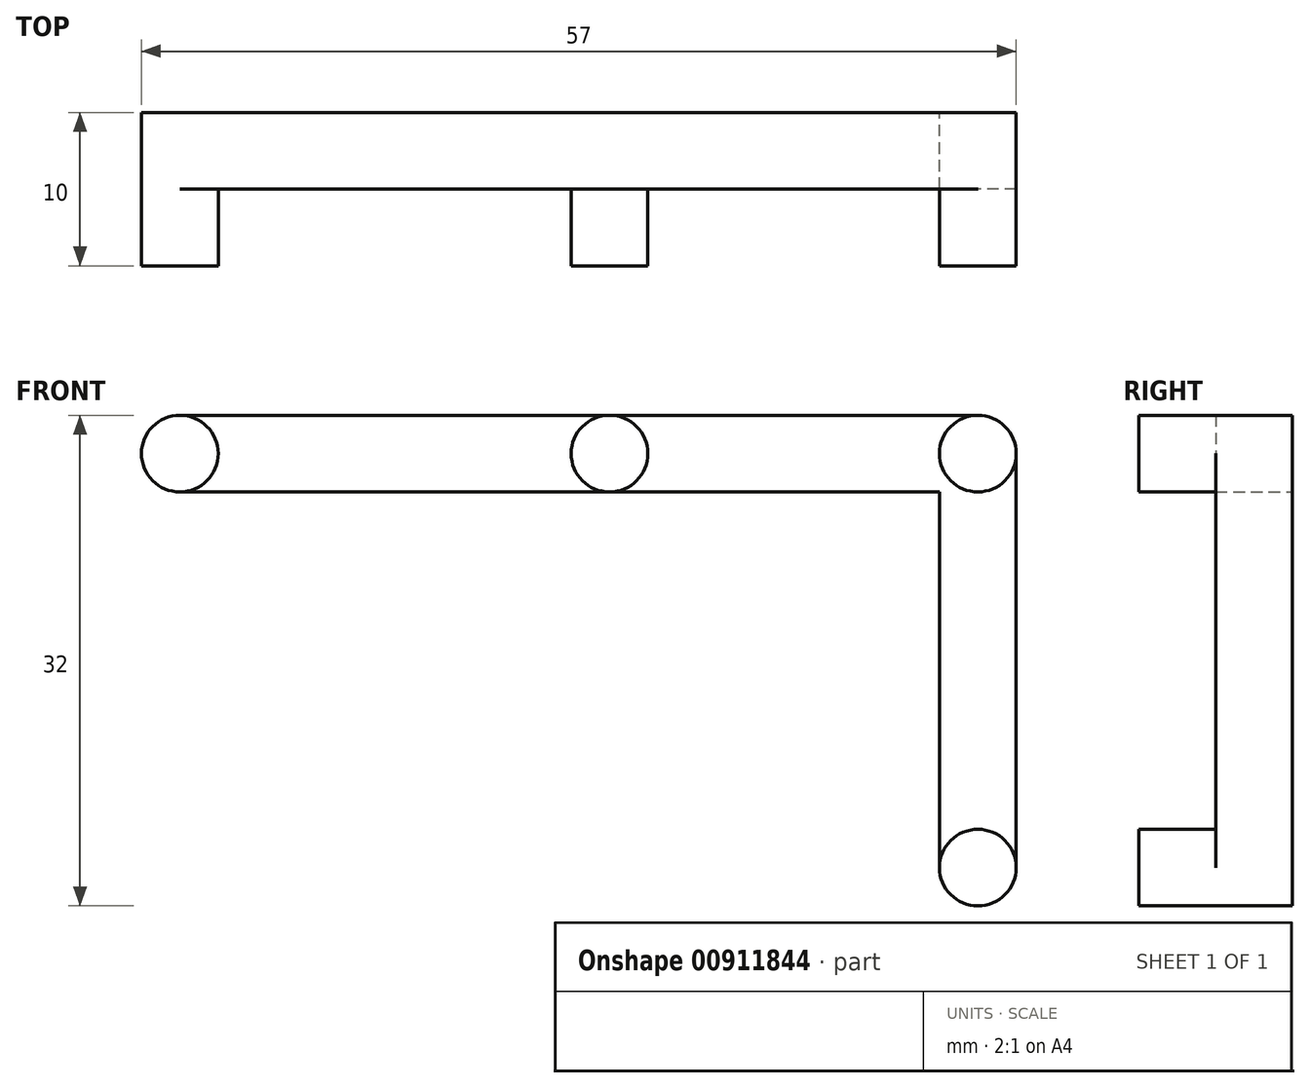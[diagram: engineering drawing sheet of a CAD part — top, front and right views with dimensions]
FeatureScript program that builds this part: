
annotation { "Feature Type Name" : "Feature", "Feature Type Description" : "" }
export const myFeature = defineFeature(function(context is Context, id is Id, definition is map)
    precondition{}
    {
        {
            var Q0;
            Q0=qCreatedBy(makeId("Front.planeOp"),FACE);
            var sketch = newSketch(context, id + "F0", { "sketchPlane" : qUnion([Q0])});
            skCircle(sketch, "E0", {"center": v(0, 0) * mm, "radius": 2.5 * mm});
            skCircle(sketch, "E1", {"center": v(28, 0) * mm, "radius": 2.5 * mm});
            skCircle(sketch, "E2", {"center": v(52, 0) * mm, "radius": 2.5 * mm});
            skCircle(sketch, "E3", {"center": v(52, -27) * mm, "radius": 2.5 * mm});
            skLineSegment(sketch, "E4.bottom", {"start": v(0, 2.5) * mm, "end": v(52, 2.5) * mm});
            skLineSegment(sketch, "E4.top", {"start": v(0, -2.5) * mm, "end": v(52, -2.5) * mm});
            skLineSegment(sketch, "E4.left", {"start": v(0, 2.5) * mm, "end": v(0, -2.5) * mm});
            skLineSegment(sketch, "E4.right", {"start": v(52, 2.5) * mm, "end": v(52, -2.5) * mm});
            skLineSegment(sketch, "E5.bottom", {"start": v(49.5, 0) * mm, "end": v(54.5, 0) * mm});
            skLineSegment(sketch, "E5.top", {"start": v(49.5, -27) * mm, "end": v(54.5, -27) * mm});
            skLineSegment(sketch, "E5.left", {"start": v(49.5, 0) * mm, "end": v(49.5, -27) * mm});
            skLineSegment(sketch, "E5.right", {"start": v(54.5, 0) * mm, "end": v(54.5, -27) * mm});
            skSolve(sketch);
        }
        {
            var Q0;
            Q0 = qSketchRegion(id + "F0", true);
            var Q1;
            {var subQ0=sQuery(id+"F0.wireOp",EDGE,"E4.right");var subQ3=sQuery(id+"F0.wireOp",EDGE,"E5.bottom");var subQ5=makeQuery(id+"F0.imprint","INTERSECT",VERTEX,{"derivedFrom":[subQ0,subQ3]});Q1=makeQuery(id+"F0.imprint","IMPRINT",FACE,{"disambiguationData":[TD([[makeQuery(id+"F0.imprint","IMPRINT",EDGE,{"disambiguationData":[TD([[subQ5,-1.0]])],"derivedFrom":subQ0}),-1.0]])]});}
            extrude(context, id + "F1", {"entities" : qUnion([Q0, Q1]), "depth" : 5 * mm, "offsetDistance" : 25 * mm});
        }
        {
            var Q0;
            {var subQ0=sQuery(id+"F0.wireOp",EDGE,"E4.left");Q0=makeQuery(id+"F0.imprint","IMPRINT",FACE,{"disambiguationData":[TD([[makeQuery(id+"F0.imprint","IMPRINT",EDGE,{"derivedFrom":subQ0}),1.0]])]});}
            var Q1;
            {var subQ0=sQuery(id+"F0.wireOp",EDGE,"E4.left");Q1=makeQuery(id+"F0.imprint","IMPRINT",FACE,{"disambiguationData":[TD([[makeQuery(id+"F0.imprint","IMPRINT",EDGE,{"derivedFrom":subQ0}),-1.0]])]});}
            var Q2;
            {var subQ0=sQuery(id+"F0.wireOp",EDGE,"E1");var subQ1=makeQuery(id+"F0.imprint","INTERSECT",VERTEX,{"derivedFrom":[subQ0,sQuery(id+"F0.wireOp",EDGE,"E4.bottom")]});Q2=makeQuery(id+"F0.imprint","IMPRINT",FACE,{"disambiguationData":[TD([[makeQuery(id+"F0.imprint","IMPRINT",EDGE,{"disambiguationData":[TD([[subQ1,-1.0]])],"derivedFrom":subQ0}),1.0]])]});}
            var Q3;
            {var subQ0=sQuery(id+"F0.wireOp",EDGE,"E4.right");var subQ3=sQuery(id+"F0.wireOp",EDGE,"E5.bottom");var subQ5=makeQuery(id+"F0.imprint","INTERSECT",VERTEX,{"derivedFrom":[subQ0,subQ3]});Q3=makeQuery(id+"F0.imprint","IMPRINT",FACE,{"disambiguationData":[TD([[makeQuery(id+"F0.imprint","IMPRINT",EDGE,{"disambiguationData":[TD([[subQ5,-1.0]])],"derivedFrom":subQ0}),-1.0]])]});}
            var Q4;
            {var subQ0=sQuery(id+"F0.wireOp",EDGE,"E4.right");var subQ3=sQuery(id+"F0.wireOp",EDGE,"E5.bottom");var subQ5=makeQuery(id+"F0.imprint","INTERSECT",VERTEX,{"derivedFrom":[subQ0,subQ3]});Q4=makeQuery(id+"F0.imprint","IMPRINT",FACE,{"disambiguationData":[TD([[makeQuery(id+"F0.imprint","IMPRINT",EDGE,{"disambiguationData":[TD([[subQ5,-1.0]])],"derivedFrom":subQ0}),1.0]])]});}
            var Q5;
            {var subQ0=sQuery(id+"F0.wireOp",EDGE,"E4.right");var subQ3=sQuery(id+"F0.wireOp",EDGE,"E5.bottom");var subQ5=makeQuery(id+"F0.imprint","INTERSECT",VERTEX,{"derivedFrom":[subQ0,subQ3]});Q5=makeQuery(id+"F0.imprint","IMPRINT",FACE,{"disambiguationData":[TD([[makeQuery(id+"F0.imprint","IMPRINT",EDGE,{"disambiguationData":[TD([[subQ5,1.0]])],"derivedFrom":subQ0}),1.0]])]});}
            var Q6;
            {var subQ0=sQuery(id+"F0.wireOp",EDGE,"E4.right");var subQ3=sQuery(id+"F0.wireOp",EDGE,"E5.bottom");var subQ5=makeQuery(id+"F0.imprint","INTERSECT",VERTEX,{"derivedFrom":[subQ0,subQ3]});Q6=makeQuery(id+"F0.imprint","IMPRINT",FACE,{"disambiguationData":[TD([[makeQuery(id+"F0.imprint","IMPRINT",EDGE,{"disambiguationData":[TD([[subQ5,1.0]])],"derivedFrom":subQ0}),-1.0]])]});}
            var Q7;
            {var subQ0=sQuery(id+"F0.wireOp",EDGE,"E5.top");Q7=makeQuery(id+"F0.imprint","IMPRINT",FACE,{"disambiguationData":[TD([[makeQuery(id+"F0.imprint","IMPRINT",EDGE,{"derivedFrom":subQ0}),1.0]])]});}
            var Q8;
            {var subQ0=sQuery(id+"F0.wireOp",EDGE,"E5.top");Q8=makeQuery(id+"F0.imprint","IMPRINT",FACE,{"disambiguationData":[TD([[makeQuery(id+"F0.imprint","IMPRINT",EDGE,{"derivedFrom":subQ0}),-1.0]])]});}
            extrude(context, id + "F2", {"entities" : qUnion([Q0, Q1, Q2, Q3, Q4, Q5, Q6, Q7, Q8]), "operationType" : NewBodyOperationType.ADD, "depth" : 10 * mm, "offsetDistance" : 25 * mm});
        }
    });
